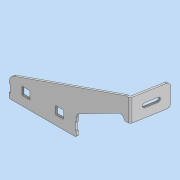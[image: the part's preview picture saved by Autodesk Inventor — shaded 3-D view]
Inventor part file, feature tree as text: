
AUTODESK INVENTOR PART (.ipt)
format: ipt  version: 2020 (Build 240168000, 168)  size: 245,760 bytes
history: native  units: mm
features: other x2, extrude x1, plane x1
ambient origin geometry x8: Origin, YZ Plane, XZ Plane, XY Plane, X Axis, Y Axis, Z Axis, Center Point
bodies: Body1 (feature_tree)
feature tree (4):
  other  "實體1"
  extrude  "擠出1"  Depth=130.0mm
  other  "折彎零件1"
  plane  "工作平面1"
